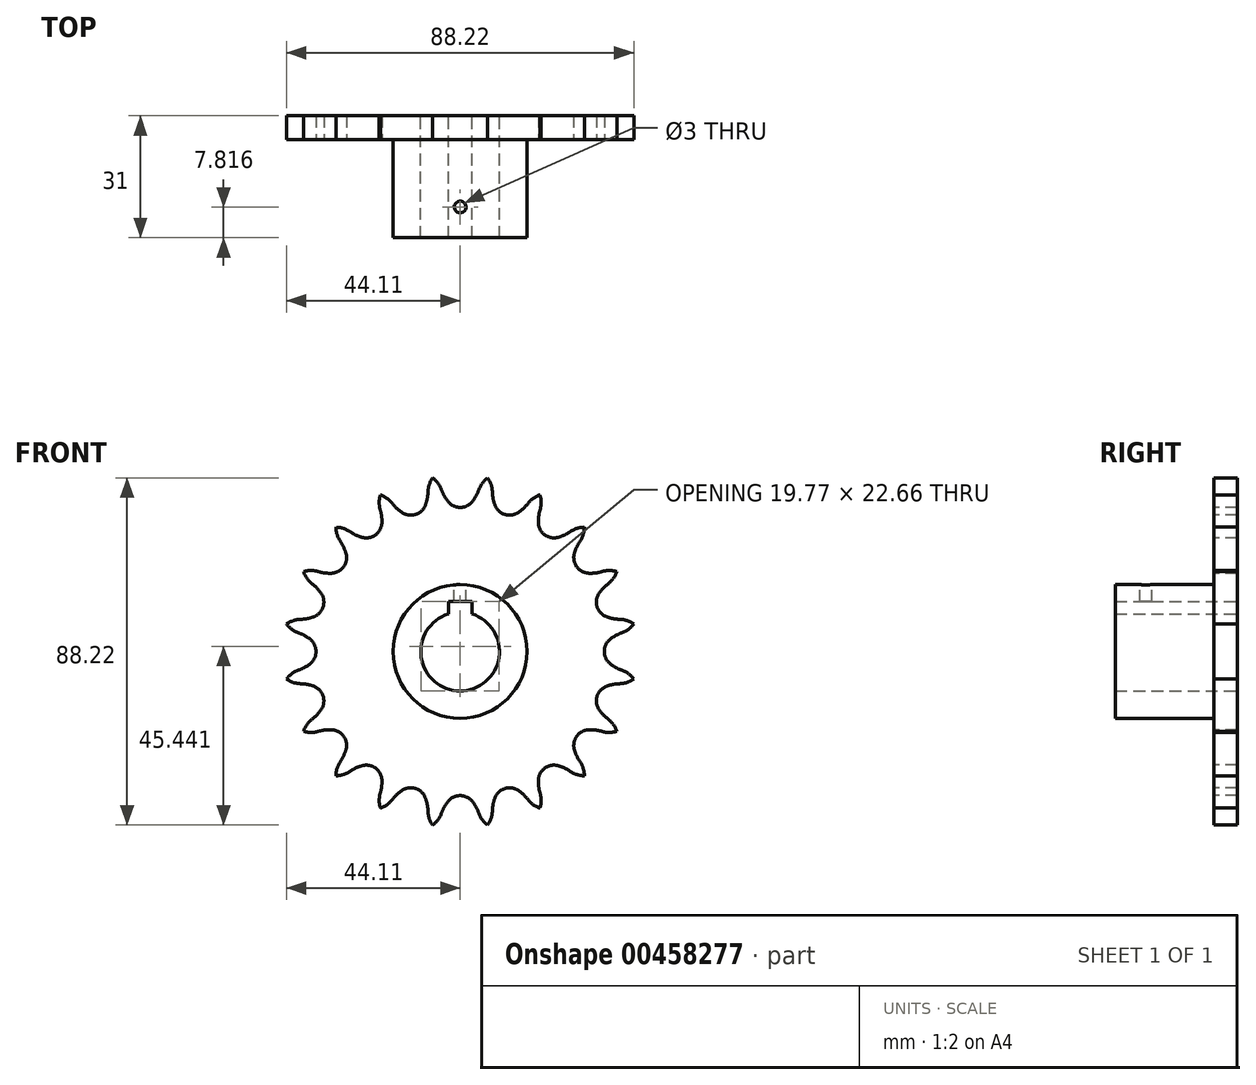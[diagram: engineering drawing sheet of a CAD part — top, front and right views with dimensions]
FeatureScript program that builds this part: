
annotation { "Feature Type Name" : "Feature", "Feature Type Description" : "" }
export const myFeature = defineFeature(function(context is Context, id is Id, definition is map)
    precondition{}
    {
        {
            var Q0;
            Q0=qCreatedBy(makeId("Front.planeOp"),FACE);
            var sketch = newSketch(context, id + "F0", { "sketchPlane" : qUnion([Q0])});
            skCircle(sketch, "E0", {"center": v(0, 0) * mm, "radius": 17 * mm});
            skArc(sketch, "E1", {"start": v(-3, 9.54) * mm, "mid": v(0, -10) * mm, "end": v(3, 9.54) * mm});
            skLineSegment(sketch, "E2.top", {"start": v(3, 12.66) * mm, "end": v(-3, 12.66) * mm});
            skLineSegment(sketch, "E2.left", {"start": v(3, 9.54) * mm, "end": v(3, 12.66) * mm});
            skLineSegment(sketch, "E2.right", {"start": v(-3, 9.54) * mm, "end": v(-3, 12.66) * mm});
            skPoint(sketch, "E2.middle", {"position": v(0, 11.1) * mm});
            skSolve(sketch);
        }
        {
            var Q0;
            Q0=makeQuery(id+"F0.imprint","IMPRINT",FACE,{"disambiguationData":[TD([[makeQuery(id+"F0.imprint","IMPRINT",EDGE,{"derivedFrom":sQuery(id+"F0.wireOp",EDGE,"E0")}),1.0]])]});
            extrude(context, id + "F1", {"entities" : qUnion([Q0]), "depth" : 25 * mm, "offsetDistance" : 25 * mm});
        }
        {
            var Q0;
            Q0=qCreatedBy(makeId("Front.planeOp"),FACE);
            var sketch = newSketch(context, id + "F2", { "sketchPlane" : qUnion([Q0])});
            skCircle(sketch, "E3", {"center": v(0, 0) * mm, "radius": 40.6 * mm, "construction": true});
            skLineSegment(sketch, "E4", {"start": v(0, 0) * mm, "end": v(0, 40.6) * mm, "construction": true});
            skLineSegment(sketch, "E5", {"start": v(0, 40.6) * mm, "end": v(64.8, 40.6) * mm, "construction": true});
            skLineSegment(sketch, "E6", {"start": v(64.8, 40.6) * mm, "end": v(-63.43, 40.6) * mm, "construction": true});
            skLineSegment(sketch, "E7", {"start": v(0, 40.6) * mm, "end": v(5, 44.5) * mm, "construction": true});
            skLineSegment(sketch, "E8", {"start": v(0, 40.6) * mm, "end": v(-3.14, 38.14) * mm, "construction": true});
            skLineSegment(sketch, "E9", {"start": v(5, 44.5) * mm, "end": v(-6.45, 39.68) * mm, "construction": true});
            skLineSegment(sketch, "E10", {"start": v(-37.34, 38.86) * mm, "end": v(-6.4, 38.86) * mm, "construction": true});
            skLineSegment(sketch, "E11", {"start": v(0, 0) * mm, "end": v(-6.99, 44.11) * mm, "construction": true});
            skArc(sketch, "E12", {"start": v(-4.53, 40.34) * mm, "mid": v(-4.62, 40.7) * mm, "end": v(-4.73, 41.05) * mm});
            skArc(sketch, "E13", {"start": v(-4.73, 41.05) * mm, "mid": v(-5.63, 42.75) * mm, "end": v(-6.99, 44.11) * mm});
            skArc(sketch, "E14", {"start": v(-4.73, 41.05) * mm, "mid": v(-4.05, 39.53) * mm, "end": v(-3.14, 38.14) * mm});
            skLineSegment(sketch, "E15", {"start": v(-3.14, 38.14) * mm, "end": v(-3.14, 38.14) * mm});
            skArc(sketch, "E16", {"start": v(3.98, 40.4) * mm, "mid": v(3.98, 40.5) * mm, "end": v(3.98, 40.6) * mm});
            skArc(sketch, "E17", {"start": v(-3.14, 38.14) * mm, "mid": v(-1.75, 37.01) * mm, "end": v(0, 36.61) * mm});
            skArc(sketch, "E18.trimOffspring", {"start": v(-3.98, 40.72) * mm, "mid": v(-3.98, 40.66) * mm, "end": v(-3.98, 40.6) * mm});
            skArc(sketch, "E19.trimOffspring", {"start": v(3.14, 43.04) * mm, "mid": v(2.92, 43.3) * mm, "end": v(2.7, 43.53) * mm});
            skArc(sketch, "E20.MirrorCS", {"start": v(3.14, 38.14) * mm, "mid": v(1.75, 37.01) * mm, "end": v(0, 36.61) * mm});
            skArc(sketch, "E21.MirrorCS", {"start": v(4.73, 41.05) * mm, "mid": v(4.05, 39.53) * mm, "end": v(3.14, 38.14) * mm});
            skArc(sketch, "E22.MirrorCS", {"start": v(4.73, 41.05) * mm, "mid": v(5.63, 42.75) * mm, "end": v(6.99, 44.11) * mm});
            skArc(sketch, "E23.1.0", {"start": v(-17.19, 37.58) * mm, "mid": v(-18.57, 38.91) * mm, "end": v(-20.28, 39.8) * mm});
            skArc(sketch, "E23.1.1", {"start": v(-17.19, 37.58) * mm, "mid": v(-16.07, 36.34) * mm, "end": v(-14.77, 35.3) * mm});
            skArc(sketch, "E23.1.2", {"start": v(-14.77, 35.3) * mm, "mid": v(-13.1, 34.66) * mm, "end": v(-11.31, 34.82) * mm});
            skArc(sketch, "E23.1.3", {"start": v(-8.8, 37.24) * mm, "mid": v(-9.78, 35.74) * mm, "end": v(-11.31, 34.82) * mm});
            skArc(sketch, "E23.1.4", {"start": v(-8.18, 40.5) * mm, "mid": v(-8.36, 38.85) * mm, "end": v(-8.8, 37.24) * mm});
            skArc(sketch, "E23.1.5", {"start": v(-8.18, 40.5) * mm, "mid": v(-7.85, 42.4) * mm, "end": v(-6.99, 44.11) * mm});
            skArc(sketch, "E23.2.0", {"start": v(-27.96, 30.43) * mm, "mid": v(-29.68, 31.27) * mm, "end": v(-31.58, 31.58) * mm});
            skArc(sketch, "E23.2.1", {"start": v(-27.96, 30.43) * mm, "mid": v(-26.51, 29.6) * mm, "end": v(-24.96, 29.01) * mm});
            skArc(sketch, "E23.2.2", {"start": v(-24.96, 29.01) * mm, "mid": v(-23.17, 28.92) * mm, "end": v(-21.52, 29.62) * mm});
            skArc(sketch, "E23.2.3", {"start": v(-19.88, 32.7) * mm, "mid": v(-20.34, 30.97) * mm, "end": v(-21.52, 29.62) * mm});
            skArc(sketch, "E23.2.4", {"start": v(-20.3, 36) * mm, "mid": v(-19.96, 34.36) * mm, "end": v(-19.88, 32.7) * mm});
            skArc(sketch, "E23.2.5", {"start": v(-20.3, 36) * mm, "mid": v(-20.57, 37.9) * mm, "end": v(-20.28, 39.8) * mm});
            skArc(sketch, "E23.3.0", {"start": v(-36, 20.3) * mm, "mid": v(-37.9, 20.57) * mm, "end": v(-39.8, 20.28) * mm});
            skArc(sketch, "E23.3.1", {"start": v(-36, 20.3) * mm, "mid": v(-34.36, 19.96) * mm, "end": v(-32.7, 19.88) * mm});
            skArc(sketch, "E23.3.2", {"start": v(-32.7, 19.88) * mm, "mid": v(-30.97, 20.34) * mm, "end": v(-29.62, 21.52) * mm});
            skArc(sketch, "E23.3.3", {"start": v(-29.01, 24.96) * mm, "mid": v(-28.92, 23.17) * mm, "end": v(-29.62, 21.52) * mm});
            skArc(sketch, "E23.3.4", {"start": v(-30.43, 27.96) * mm, "mid": v(-29.6, 26.51) * mm, "end": v(-29.01, 24.96) * mm});
            skArc(sketch, "E23.3.5", {"start": v(-30.43, 27.96) * mm, "mid": v(-31.27, 29.68) * mm, "end": v(-31.58, 31.58) * mm});
            skArc(sketch, "E23.4.0", {"start": v(-40.5, 8.18) * mm, "mid": v(-42.4, 7.85) * mm, "end": v(-44.11, 6.99) * mm});
            skArc(sketch, "E23.4.1", {"start": v(-40.5, 8.18) * mm, "mid": v(-38.85, 8.36) * mm, "end": v(-37.24, 8.8) * mm});
            skArc(sketch, "E23.4.2", {"start": v(-37.24, 8.8) * mm, "mid": v(-35.74, 9.78) * mm, "end": v(-34.82, 11.31) * mm});
            skArc(sketch, "E23.4.3", {"start": v(-35.3, 14.77) * mm, "mid": v(-34.66, 13.1) * mm, "end": v(-34.82, 11.31) * mm});
            skArc(sketch, "E23.4.4", {"start": v(-37.58, 17.19) * mm, "mid": v(-36.34, 16.07) * mm, "end": v(-35.3, 14.77) * mm});
            skArc(sketch, "E23.4.5", {"start": v(-37.58, 17.19) * mm, "mid": v(-38.91, 18.57) * mm, "end": v(-39.8, 20.28) * mm});
            skArc(sketch, "E23.5.0", {"start": v(-41.05, -4.73) * mm, "mid": v(-42.75, -5.63) * mm, "end": v(-44.11, -6.99) * mm});
            skArc(sketch, "E23.5.1", {"start": v(-41.05, -4.73) * mm, "mid": v(-39.53, -4.05) * mm, "end": v(-38.14, -3.14) * mm});
            skArc(sketch, "E23.5.2", {"start": v(-38.14, -3.14) * mm, "mid": v(-37.01, -1.75) * mm, "end": v(-36.61, 0) * mm});
            skArc(sketch, "E23.5.3", {"start": v(-38.14, 3.14) * mm, "mid": v(-37.01, 1.75) * mm, "end": v(-36.61, 0) * mm});
            skArc(sketch, "E23.5.4", {"start": v(-41.05, 4.73) * mm, "mid": v(-39.53, 4.05) * mm, "end": v(-38.14, 3.14) * mm});
            skArc(sketch, "E23.5.5", {"start": v(-41.05, 4.73) * mm, "mid": v(-42.75, 5.63) * mm, "end": v(-44.11, 6.99) * mm});
            skArc(sketch, "E23.6.0", {"start": v(-37.58, -17.19) * mm, "mid": v(-38.91, -18.57) * mm, "end": v(-39.8, -20.28) * mm});
            skArc(sketch, "E23.6.1", {"start": v(-37.58, -17.19) * mm, "mid": v(-36.34, -16.07) * mm, "end": v(-35.3, -14.77) * mm});
            skArc(sketch, "E23.6.2", {"start": v(-35.3, -14.77) * mm, "mid": v(-34.66, -13.1) * mm, "end": v(-34.82, -11.31) * mm});
            skArc(sketch, "E23.6.3", {"start": v(-37.24, -8.8) * mm, "mid": v(-35.74, -9.78) * mm, "end": v(-34.82, -11.31) * mm});
            skArc(sketch, "E23.6.4", {"start": v(-40.5, -8.18) * mm, "mid": v(-38.85, -8.36) * mm, "end": v(-37.24, -8.8) * mm});
            skArc(sketch, "E23.6.5", {"start": v(-40.5, -8.18) * mm, "mid": v(-42.4, -7.85) * mm, "end": v(-44.11, -6.99) * mm});
            skArc(sketch, "E23.7.0", {"start": v(-30.43, -27.96) * mm, "mid": v(-31.27, -29.68) * mm, "end": v(-31.58, -31.58) * mm});
            skArc(sketch, "E23.7.1", {"start": v(-30.43, -27.96) * mm, "mid": v(-29.6, -26.51) * mm, "end": v(-29.01, -24.96) * mm});
            skArc(sketch, "E23.7.2", {"start": v(-29.01, -24.96) * mm, "mid": v(-28.92, -23.17) * mm, "end": v(-29.62, -21.52) * mm});
            skArc(sketch, "E23.7.3", {"start": v(-32.7, -19.88) * mm, "mid": v(-30.97, -20.34) * mm, "end": v(-29.62, -21.52) * mm});
            skArc(sketch, "E23.7.4", {"start": v(-36, -20.3) * mm, "mid": v(-34.36, -19.96) * mm, "end": v(-32.7, -19.88) * mm});
            skArc(sketch, "E23.7.5", {"start": v(-36, -20.3) * mm, "mid": v(-37.9, -20.57) * mm, "end": v(-39.8, -20.28) * mm});
            skArc(sketch, "E23.8.0", {"start": v(-20.3, -36) * mm, "mid": v(-20.57, -37.9) * mm, "end": v(-20.28, -39.8) * mm});
            skArc(sketch, "E23.8.1", {"start": v(-20.3, -36) * mm, "mid": v(-19.96, -34.36) * mm, "end": v(-19.88, -32.7) * mm});
            skArc(sketch, "E23.8.2", {"start": v(-19.88, -32.7) * mm, "mid": v(-20.34, -30.97) * mm, "end": v(-21.52, -29.62) * mm});
            skArc(sketch, "E23.8.3", {"start": v(-24.96, -29.01) * mm, "mid": v(-23.17, -28.92) * mm, "end": v(-21.52, -29.62) * mm});
            skArc(sketch, "E23.8.4", {"start": v(-27.96, -30.43) * mm, "mid": v(-26.51, -29.6) * mm, "end": v(-24.96, -29.01) * mm});
            skArc(sketch, "E23.8.5", {"start": v(-27.96, -30.43) * mm, "mid": v(-29.68, -31.27) * mm, "end": v(-31.58, -31.58) * mm});
            skArc(sketch, "E23.9.0", {"start": v(-8.18, -40.5) * mm, "mid": v(-7.85, -42.4) * mm, "end": v(-6.99, -44.11) * mm});
            skArc(sketch, "E23.9.1", {"start": v(-8.18, -40.5) * mm, "mid": v(-8.36, -38.85) * mm, "end": v(-8.8, -37.24) * mm});
            skArc(sketch, "E23.9.2", {"start": v(-8.8, -37.24) * mm, "mid": v(-9.78, -35.74) * mm, "end": v(-11.31, -34.82) * mm});
            skArc(sketch, "E23.9.3", {"start": v(-14.77, -35.3) * mm, "mid": v(-13.1, -34.66) * mm, "end": v(-11.31, -34.82) * mm});
            skArc(sketch, "E23.9.4", {"start": v(-17.19, -37.58) * mm, "mid": v(-16.07, -36.34) * mm, "end": v(-14.77, -35.3) * mm});
            skArc(sketch, "E23.9.5", {"start": v(-17.19, -37.58) * mm, "mid": v(-18.57, -38.91) * mm, "end": v(-20.28, -39.8) * mm});
            skArc(sketch, "E23.10.0", {"start": v(4.73, -41.05) * mm, "mid": v(5.63, -42.75) * mm, "end": v(6.99, -44.11) * mm});
            skArc(sketch, "E23.10.1", {"start": v(4.73, -41.05) * mm, "mid": v(4.05, -39.53) * mm, "end": v(3.14, -38.14) * mm});
            skArc(sketch, "E23.10.2", {"start": v(3.14, -38.14) * mm, "mid": v(1.75, -37.01) * mm, "end": v(0, -36.61) * mm});
            skArc(sketch, "E23.10.3", {"start": v(-3.14, -38.14) * mm, "mid": v(-1.75, -37.01) * mm, "end": v(0, -36.61) * mm});
            skArc(sketch, "E23.10.4", {"start": v(-4.73, -41.05) * mm, "mid": v(-4.05, -39.53) * mm, "end": v(-3.14, -38.14) * mm});
            skArc(sketch, "E23.10.5", {"start": v(-4.73, -41.05) * mm, "mid": v(-5.63, -42.75) * mm, "end": v(-6.99, -44.11) * mm});
            skArc(sketch, "E23.11.0", {"start": v(17.19, -37.58) * mm, "mid": v(18.57, -38.91) * mm, "end": v(20.28, -39.8) * mm});
            skArc(sketch, "E23.11.1", {"start": v(17.19, -37.58) * mm, "mid": v(16.07, -36.34) * mm, "end": v(14.77, -35.3) * mm});
            skArc(sketch, "E23.11.2", {"start": v(14.77, -35.3) * mm, "mid": v(13.1, -34.66) * mm, "end": v(11.31, -34.82) * mm});
            skArc(sketch, "E23.11.3", {"start": v(8.8, -37.24) * mm, "mid": v(9.78, -35.74) * mm, "end": v(11.31, -34.82) * mm});
            skArc(sketch, "E23.11.4", {"start": v(8.18, -40.5) * mm, "mid": v(8.36, -38.85) * mm, "end": v(8.8, -37.24) * mm});
            skArc(sketch, "E23.11.5", {"start": v(8.18, -40.5) * mm, "mid": v(7.85, -42.4) * mm, "end": v(6.99, -44.11) * mm});
            skArc(sketch, "E23.12.0", {"start": v(27.96, -30.43) * mm, "mid": v(29.68, -31.27) * mm, "end": v(31.58, -31.58) * mm});
            skArc(sketch, "E23.12.1", {"start": v(27.96, -30.43) * mm, "mid": v(26.51, -29.6) * mm, "end": v(24.96, -29.01) * mm});
            skArc(sketch, "E23.12.2", {"start": v(24.96, -29.01) * mm, "mid": v(23.17, -28.92) * mm, "end": v(21.52, -29.62) * mm});
            skArc(sketch, "E23.12.3", {"start": v(19.88, -32.7) * mm, "mid": v(20.34, -30.97) * mm, "end": v(21.52, -29.62) * mm});
            skArc(sketch, "E23.12.4", {"start": v(20.3, -36) * mm, "mid": v(19.96, -34.36) * mm, "end": v(19.88, -32.7) * mm});
            skArc(sketch, "E23.12.5", {"start": v(20.3, -36) * mm, "mid": v(20.57, -37.9) * mm, "end": v(20.28, -39.8) * mm});
            skArc(sketch, "E23.13.0", {"start": v(36, -20.3) * mm, "mid": v(37.9, -20.57) * mm, "end": v(39.8, -20.28) * mm});
            skArc(sketch, "E23.13.1", {"start": v(36, -20.3) * mm, "mid": v(34.36, -19.96) * mm, "end": v(32.7, -19.88) * mm});
            skArc(sketch, "E23.13.2", {"start": v(32.7, -19.88) * mm, "mid": v(30.97, -20.34) * mm, "end": v(29.62, -21.52) * mm});
            skArc(sketch, "E23.13.3", {"start": v(29.01, -24.96) * mm, "mid": v(28.92, -23.17) * mm, "end": v(29.62, -21.52) * mm});
            skArc(sketch, "E23.13.4", {"start": v(30.43, -27.96) * mm, "mid": v(29.6, -26.51) * mm, "end": v(29.01, -24.96) * mm});
            skArc(sketch, "E23.13.5", {"start": v(30.43, -27.96) * mm, "mid": v(31.27, -29.68) * mm, "end": v(31.58, -31.58) * mm});
            skArc(sketch, "E23.14.0", {"start": v(40.5, -8.18) * mm, "mid": v(42.4, -7.85) * mm, "end": v(44.11, -6.99) * mm});
            skArc(sketch, "E23.14.1", {"start": v(40.5, -8.18) * mm, "mid": v(38.85, -8.36) * mm, "end": v(37.24, -8.8) * mm});
            skArc(sketch, "E23.14.2", {"start": v(37.24, -8.8) * mm, "mid": v(35.74, -9.78) * mm, "end": v(34.82, -11.31) * mm});
            skArc(sketch, "E23.14.3", {"start": v(35.3, -14.77) * mm, "mid": v(34.66, -13.1) * mm, "end": v(34.82, -11.31) * mm});
            skArc(sketch, "E23.14.4", {"start": v(37.58, -17.19) * mm, "mid": v(36.34, -16.07) * mm, "end": v(35.3, -14.77) * mm});
            skArc(sketch, "E23.14.5", {"start": v(37.58, -17.19) * mm, "mid": v(38.91, -18.57) * mm, "end": v(39.8, -20.28) * mm});
            skArc(sketch, "E23.15.0", {"start": v(41.05, 4.73) * mm, "mid": v(42.75, 5.63) * mm, "end": v(44.11, 6.99) * mm});
            skArc(sketch, "E23.15.1", {"start": v(41.05, 4.73) * mm, "mid": v(39.53, 4.05) * mm, "end": v(38.14, 3.14) * mm});
            skArc(sketch, "E23.15.2", {"start": v(38.14, 3.14) * mm, "mid": v(37.01, 1.75) * mm, "end": v(36.61, 0) * mm});
            skArc(sketch, "E23.15.3", {"start": v(38.14, -3.14) * mm, "mid": v(37.01, -1.75) * mm, "end": v(36.61, 0) * mm});
            skArc(sketch, "E23.15.4", {"start": v(41.05, -4.73) * mm, "mid": v(39.53, -4.05) * mm, "end": v(38.14, -3.14) * mm});
            skArc(sketch, "E23.15.5", {"start": v(41.05, -4.73) * mm, "mid": v(42.75, -5.63) * mm, "end": v(44.11, -6.99) * mm});
            skArc(sketch, "E23.16.0", {"start": v(37.58, 17.19) * mm, "mid": v(38.91, 18.57) * mm, "end": v(39.8, 20.28) * mm});
            skArc(sketch, "E23.16.1", {"start": v(37.58, 17.19) * mm, "mid": v(36.34, 16.07) * mm, "end": v(35.3, 14.77) * mm});
            skArc(sketch, "E23.16.2", {"start": v(35.3, 14.77) * mm, "mid": v(34.66, 13.1) * mm, "end": v(34.82, 11.31) * mm});
            skArc(sketch, "E23.16.3", {"start": v(37.24, 8.8) * mm, "mid": v(35.74, 9.78) * mm, "end": v(34.82, 11.31) * mm});
            skArc(sketch, "E23.16.4", {"start": v(40.5, 8.18) * mm, "mid": v(38.85, 8.36) * mm, "end": v(37.24, 8.8) * mm});
            skArc(sketch, "E23.16.5", {"start": v(40.5, 8.18) * mm, "mid": v(42.4, 7.85) * mm, "end": v(44.11, 6.99) * mm});
            skArc(sketch, "E23.17.0", {"start": v(30.43, 27.96) * mm, "mid": v(31.27, 29.68) * mm, "end": v(31.58, 31.58) * mm});
            skArc(sketch, "E23.17.1", {"start": v(30.43, 27.96) * mm, "mid": v(29.6, 26.51) * mm, "end": v(29.01, 24.96) * mm});
            skArc(sketch, "E23.17.2", {"start": v(29.01, 24.96) * mm, "mid": v(28.92, 23.17) * mm, "end": v(29.62, 21.52) * mm});
            skArc(sketch, "E23.17.3", {"start": v(32.7, 19.88) * mm, "mid": v(30.97, 20.34) * mm, "end": v(29.62, 21.52) * mm});
            skArc(sketch, "E23.17.4", {"start": v(36, 20.3) * mm, "mid": v(34.36, 19.96) * mm, "end": v(32.7, 19.88) * mm});
            skArc(sketch, "E23.17.5", {"start": v(36, 20.3) * mm, "mid": v(37.9, 20.57) * mm, "end": v(39.8, 20.28) * mm});
            skArc(sketch, "E23.18.0", {"start": v(20.3, 36) * mm, "mid": v(20.57, 37.9) * mm, "end": v(20.28, 39.8) * mm});
            skArc(sketch, "E23.18.1", {"start": v(20.3, 36) * mm, "mid": v(19.96, 34.36) * mm, "end": v(19.88, 32.7) * mm});
            skArc(sketch, "E23.18.2", {"start": v(19.88, 32.7) * mm, "mid": v(20.34, 30.97) * mm, "end": v(21.52, 29.62) * mm});
            skArc(sketch, "E23.18.3", {"start": v(24.96, 29.01) * mm, "mid": v(23.17, 28.92) * mm, "end": v(21.52, 29.62) * mm});
            skArc(sketch, "E23.18.4", {"start": v(27.96, 30.43) * mm, "mid": v(26.51, 29.6) * mm, "end": v(24.96, 29.01) * mm});
            skArc(sketch, "E23.18.5", {"start": v(27.96, 30.43) * mm, "mid": v(29.68, 31.27) * mm, "end": v(31.58, 31.58) * mm});
            skArc(sketch, "E23.19.0", {"start": v(8.18, 40.5) * mm, "mid": v(7.85, 42.4) * mm, "end": v(6.99, 44.11) * mm});
            skArc(sketch, "E23.19.1", {"start": v(8.18, 40.5) * mm, "mid": v(8.36, 38.85) * mm, "end": v(8.8, 37.24) * mm});
            skArc(sketch, "E23.19.2", {"start": v(8.8, 37.24) * mm, "mid": v(9.78, 35.74) * mm, "end": v(11.31, 34.82) * mm});
            skArc(sketch, "E23.19.3", {"start": v(14.77, 35.3) * mm, "mid": v(13.1, 34.66) * mm, "end": v(11.31, 34.82) * mm});
            skArc(sketch, "E23.19.4", {"start": v(17.19, 37.58) * mm, "mid": v(16.07, 36.34) * mm, "end": v(14.77, 35.3) * mm});
            skArc(sketch, "E23.19.5", {"start": v(17.19, 37.58) * mm, "mid": v(18.57, 38.91) * mm, "end": v(20.28, 39.8) * mm});
            skSolve(sketch);
        }
        {
            var Q0;
            Q0=makeQuery(id+"F2.imprint","IMPRINT",FACE,{"disambiguationData":[TD([[makeQuery(id+"F2.imprint","IMPRINT",EDGE,{"derivedFrom":sQuery(id+"F2.wireOp",EDGE,"E13")}),1.0]])]});
            extrude(context, id + "F3", {"entities" : qUnion([Q0]), "operationType" : NewBodyOperationType.ADD, "oppositeDirection" : true, "depth" : 6 * mm, "offsetDistance" : 25 * mm});
        }
        {
            var Q0;
            Q0=makeQuery(id+"F3.boolean.opBoolean","SPLIT",FACE,{"disambiguationData":[TD([makeQuery(id+"F1.opExtrude","SWEPT_FACE",FACE,{"disambiguationData":[OSD([sQuery(id+"F0.wireOp",EDGE,"E1")])]})])],"derivedFrom":makeQuery(id+"F3.opExtrude","CAP_FACE",FACE,{"disambiguationData":[OSD([sQuery(id+"F2.wireOp",EDGE,"E13"),sQuery(id+"F2.wireOp",EDGE,"E14"),sQuery(id+"F2.wireOp",EDGE,"E17"),sQuery(id+"F2.wireOp",EDGE,"E20.MirrorCS"),sQuery(id+"F2.wireOp",EDGE,"E21.MirrorCS"),sQuery(id+"F2.wireOp",EDGE,"E22.MirrorCS"),sQuery(id+"F2.wireOp",EDGE,"E23.1.0"),sQuery(id+"F2.wireOp",EDGE,"E23.1.1"),sQuery(id+"F2.wireOp",EDGE,"E23.1.2"),sQuery(id+"F2.wireOp",EDGE,"E23.1.3"),sQuery(id+"F2.wireOp",EDGE,"E23.1.4"),sQuery(id+"F2.wireOp",EDGE,"E23.1.5"),sQuery(id+"F2.wireOp",EDGE,"E23.2.0"),sQuery(id+"F2.wireOp",EDGE,"E23.2.1"),sQuery(id+"F2.wireOp",EDGE,"E23.2.2"),sQuery(id+"F2.wireOp",EDGE,"E23.2.3"),sQuery(id+"F2.wireOp",EDGE,"E23.2.4"),sQuery(id+"F2.wireOp",EDGE,"E23.2.5"),sQuery(id+"F2.wireOp",EDGE,"E23.3.0"),sQuery(id+"F2.wireOp",EDGE,"E23.3.1"),sQuery(id+"F2.wireOp",EDGE,"E23.3.2"),sQuery(id+"F2.wireOp",EDGE,"E23.3.3"),sQuery(id+"F2.wireOp",EDGE,"E23.3.4"),sQuery(id+"F2.wireOp",EDGE,"E23.3.5"),sQuery(id+"F2.wireOp",EDGE,"E23.4.0"),sQuery(id+"F2.wireOp",EDGE,"E23.4.1"),sQuery(id+"F2.wireOp",EDGE,"E23.4.2"),sQuery(id+"F2.wireOp",EDGE,"E23.4.3"),sQuery(id+"F2.wireOp",EDGE,"E23.4.4"),sQuery(id+"F2.wireOp",EDGE,"E23.4.5"),sQuery(id+"F2.wireOp",EDGE,"E23.5.0"),sQuery(id+"F2.wireOp",EDGE,"E23.5.1"),sQuery(id+"F2.wireOp",EDGE,"E23.5.2"),sQuery(id+"F2.wireOp",EDGE,"E23.5.3"),sQuery(id+"F2.wireOp",EDGE,"E23.5.4"),sQuery(id+"F2.wireOp",EDGE,"E23.5.5"),sQuery(id+"F2.wireOp",EDGE,"E23.6.0"),sQuery(id+"F2.wireOp",EDGE,"E23.6.1"),sQuery(id+"F2.wireOp",EDGE,"E23.6.2"),sQuery(id+"F2.wireOp",EDGE,"E23.6.3"),sQuery(id+"F2.wireOp",EDGE,"E23.6.4"),sQuery(id+"F2.wireOp",EDGE,"E23.6.5"),sQuery(id+"F2.wireOp",EDGE,"E23.7.0"),sQuery(id+"F2.wireOp",EDGE,"E23.7.1"),sQuery(id+"F2.wireOp",EDGE,"E23.7.2"),sQuery(id+"F2.wireOp",EDGE,"E23.7.3"),sQuery(id+"F2.wireOp",EDGE,"E23.7.4"),sQuery(id+"F2.wireOp",EDGE,"E23.7.5"),sQuery(id+"F2.wireOp",EDGE,"E23.8.0"),sQuery(id+"F2.wireOp",EDGE,"E23.8.1"),sQuery(id+"F2.wireOp",EDGE,"E23.8.2"),sQuery(id+"F2.wireOp",EDGE,"E23.8.3"),sQuery(id+"F2.wireOp",EDGE,"E23.8.4"),sQuery(id+"F2.wireOp",EDGE,"E23.8.5"),sQuery(id+"F2.wireOp",EDGE,"E23.9.0"),sQuery(id+"F2.wireOp",EDGE,"E23.9.1"),sQuery(id+"F2.wireOp",EDGE,"E23.9.2"),sQuery(id+"F2.wireOp",EDGE,"E23.9.3"),sQuery(id+"F2.wireOp",EDGE,"E23.9.4"),sQuery(id+"F2.wireOp",EDGE,"E23.9.5"),sQuery(id+"F2.wireOp",EDGE,"E23.10.0"),sQuery(id+"F2.wireOp",EDGE,"E23.10.1"),sQuery(id+"F2.wireOp",EDGE,"E23.10.2"),sQuery(id+"F2.wireOp",EDGE,"E23.10.3"),sQuery(id+"F2.wireOp",EDGE,"E23.10.4"),sQuery(id+"F2.wireOp",EDGE,"E23.10.5"),sQuery(id+"F2.wireOp",EDGE,"E23.11.0"),sQuery(id+"F2.wireOp",EDGE,"E23.11.1"),sQuery(id+"F2.wireOp",EDGE,"E23.11.2"),sQuery(id+"F2.wireOp",EDGE,"E23.11.3"),sQuery(id+"F2.wireOp",EDGE,"E23.11.4"),sQuery(id+"F2.wireOp",EDGE,"E23.11.5"),sQuery(id+"F2.wireOp",EDGE,"E23.12.0"),sQuery(id+"F2.wireOp",EDGE,"E23.12.1"),sQuery(id+"F2.wireOp",EDGE,"E23.12.2"),sQuery(id+"F2.wireOp",EDGE,"E23.12.3"),sQuery(id+"F2.wireOp",EDGE,"E23.12.4"),sQuery(id+"F2.wireOp",EDGE,"E23.12.5"),sQuery(id+"F2.wireOp",EDGE,"E23.13.0"),sQuery(id+"F2.wireOp",EDGE,"E23.13.1"),sQuery(id+"F2.wireOp",EDGE,"E23.13.2"),sQuery(id+"F2.wireOp",EDGE,"E23.13.3"),sQuery(id+"F2.wireOp",EDGE,"E23.13.4"),sQuery(id+"F2.wireOp",EDGE,"E23.13.5"),sQuery(id+"F2.wireOp",EDGE,"E23.14.0"),sQuery(id+"F2.wireOp",EDGE,"E23.14.1"),sQuery(id+"F2.wireOp",EDGE,"E23.14.2"),sQuery(id+"F2.wireOp",EDGE,"E23.14.3"),sQuery(id+"F2.wireOp",EDGE,"E23.14.4"),sQuery(id+"F2.wireOp",EDGE,"E23.14.5"),sQuery(id+"F2.wireOp",EDGE,"E23.15.0"),sQuery(id+"F2.wireOp",EDGE,"E23.15.1"),sQuery(id+"F2.wireOp",EDGE,"E23.15.2"),sQuery(id+"F2.wireOp",EDGE,"E23.15.3"),sQuery(id+"F2.wireOp",EDGE,"E23.15.4"),sQuery(id+"F2.wireOp",EDGE,"E23.15.5"),sQuery(id+"F2.wireOp",EDGE,"E23.16.0"),sQuery(id+"F2.wireOp",EDGE,"E23.16.1"),sQuery(id+"F2.wireOp",EDGE,"E23.16.2"),sQuery(id+"F2.wireOp",EDGE,"E23.16.3"),sQuery(id+"F2.wireOp",EDGE,"E23.16.4"),sQuery(id+"F2.wireOp",EDGE,"E23.16.5"),sQuery(id+"F2.wireOp",EDGE,"E23.17.0"),sQuery(id+"F2.wireOp",EDGE,"E23.17.1"),sQuery(id+"F2.wireOp",EDGE,"E23.17.2"),sQuery(id+"F2.wireOp",EDGE,"E23.17.3"),sQuery(id+"F2.wireOp",EDGE,"E23.17.4"),sQuery(id+"F2.wireOp",EDGE,"E23.17.5"),sQuery(id+"F2.wireOp",EDGE,"E23.18.0"),sQuery(id+"F2.wireOp",EDGE,"E23.18.1"),sQuery(id+"F2.wireOp",EDGE,"E23.18.2"),sQuery(id+"F2.wireOp",EDGE,"E23.18.3"),sQuery(id+"F2.wireOp",EDGE,"E23.18.4"),sQuery(id+"F2.wireOp",EDGE,"E23.18.5"),sQuery(id+"F2.wireOp",EDGE,"E23.19.0"),sQuery(id+"F2.wireOp",EDGE,"E23.19.1"),sQuery(id+"F2.wireOp",EDGE,"E23.19.2"),sQuery(id+"F2.wireOp",EDGE,"E23.19.3"),sQuery(id+"F2.wireOp",EDGE,"E23.19.4"),sQuery(id+"F2.wireOp",EDGE,"E23.19.5")])],"isStart":true})});
            extrude(context, id + "F4", {"entities" : qUnion([Q0]), "operationType" : NewBodyOperationType.REMOVE, "oppositeDirection" : true, "depth" : 25 * mm, "offsetDistance" : 25 * mm});
        }
        {
            var Q0;
            Q0=qCreatedBy(makeId("Top.planeOp"),FACE);
            cPlane(context, id + "F5", {"entities" : qUnion([Q0]), "cplaneType" : CPlaneType.OFFSET, "offset" : 17 * mm, "width" : 150 * mm, "height" : 150 * mm});
        }
        {
            var Q0;
            Q0=qCreatedBy(id+"F5.planeOp",FACE);
            var sketch = newSketch(context, id + "F6", { "sketchPlane" : qUnion([Q0])});
            skLineSegment(sketch, "E24", {"start": v(0, -17.18) * mm, "end": v(0, -25.18) * mm, "construction": true});
            skCircle(sketch, "E25", {"center": v(0, -17.18) * mm, "radius": 1.5 * mm});
            skSolve(sketch);
        }
        {
            var Q0;
            Q0=makeQuery(id+"F6.imprint","IMPRINT",FACE,{"disambiguationData":[TD([[makeQuery(id+"F6.imprint","IMPRINT",EDGE,{"derivedFrom":sQuery(id+"F6.wireOp",EDGE,"E25")}),1.0]])]});
            extrude(context, id + "F7", {"entities" : qUnion([Q0]), "operationType" : NewBodyOperationType.REMOVE, "oppositeDirection" : true, "depth" : 11.1 * mm, "offsetDistance" : 25 * mm});
        }
    });
